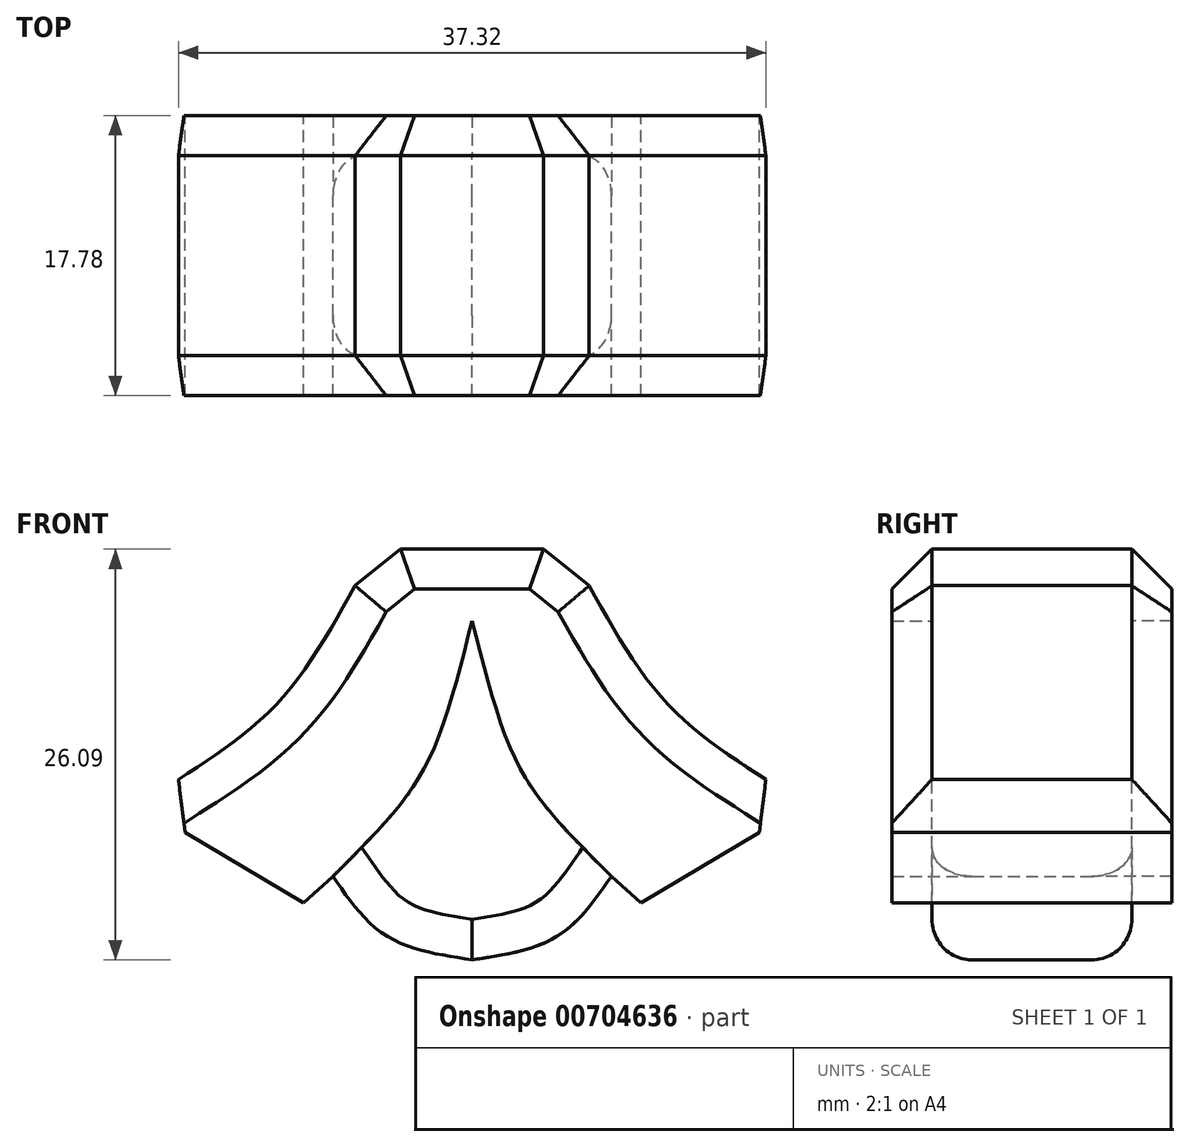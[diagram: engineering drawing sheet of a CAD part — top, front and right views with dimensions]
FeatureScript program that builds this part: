
annotation { "Feature Type Name" : "Feature", "Feature Type Description" : "" }
export const myFeature = defineFeature(function(context is Context, id is Id, definition is map)
    precondition{}
    {
        {
            var Q0;
            Q0=qCreatedBy(makeId("Front.planeOp"),FACE);
            var sketch = newSketch(context, id + "F0", { "sketchPlane" : qUnion([Q0])});
            skFitSpline(sketch, "E0", {"points": [v(-18.66, -145.03) * mm, v(-12.41, -140.25) * mm, v(-7.43, -132.73) * mm], "startDerivative": vector(13.73, 8.78) * mm, "endDerivative": vector(8.77, 15.73) * mm});
            skFitSpline(sketch, "E1", {"points": [v(0, -156.5) * mm, v(-5.42, -154.99) * mm, v(-8.85, -151.2) * mm], "startDerivative": vector(-11.5, 1.7) * mm, "endDerivative": vector(-6.16, 8.95) * mm});
            skFitSpline(sketch, "E2", {"points": [v(-6.32, -27.2) * mm, v(-15.28, -19.21) * mm, v(-26.43, -12.1) * mm, v(-37.33, -8.05) * mm], "startDerivative": vector(-25.96, 24.63) * mm, "endDerivative": vector(-33.62, 10.63) * mm});
            skFitSpline(sketch, "E3", {"points": [v(-37.33, -3.8) * mm, v(-39.84, -2.96) * mm, v(-42.51, -2.04) * mm, v(-42.5, -2) * mm], "startDerivative": vector(-4.66, 1.6) * mm, "endDerivative": vector(0.46, 0.6) * mm});
            skFitSpline(sketch, "E4", {"points": [v(-42.5, -2) * mm, v(-36.56, 4.25) * mm, v(-31.56, 12.84) * mm], "startDerivative": vector(12.98, 12.08) * mm, "endDerivative": vector(8.97, 17.54) * mm});
            skFitSpline(sketch, "E5", {"points": [v(-31.56, 12.84) * mm, v(-28.75, 11.67) * mm, v(-26.43, 10.32) * mm], "startDerivative": vector(5.62, -2.14) * mm, "endDerivative": vector(4.63, -2.93) * mm});
            skFitSpline(sketch, "E6", {"points": [v(-23.95, 12.84) * mm, v(-17.54, 8.59) * mm, v(-10.17, 1.5) * mm], "startDerivative": vector(13.82, -8.22) * mm, "endDerivative": vector(13.74, -14.33) * mm});
            skLineSegment(sketch, "E7", {"start": v(-10.17, 1.5) * mm, "end": v(0, 17.06) * mm});
            skLineSegment(sketch, "E8", {"start": v(0, 17.06) * mm, "end": v(0, 9.54) * mm});
            skLineSegment(sketch, "E9", {"start": v(0, 9.54) * mm, "end": v(0, 17.06) * mm});
            skLineSegment(sketch, "E10", {"start": v(-37.33, -3.8) * mm, "end": v(-37.33, -8.05) * mm});
            skLineSegment(sketch, "E11", {"start": v(-23.95, 12.84) * mm, "end": v(-26.43, 10.32) * mm});
            skLineSegment(sketch, "E12", {"start": v(-6.32, -27.2) * mm, "end": v(0, -29.82) * mm});
            skLineSegment(sketch, "E13", {"start": v(0, -29.82) * mm, "end": v(-6.32, -27.2) * mm});
            skLineSegment(sketch, "E14", {"start": v(-7.43, -132.73) * mm, "end": v(-4.54, -130.41) * mm});
            skLineSegment(sketch, "E15", {"start": v(-4.54, -130.41) * mm, "end": v(0, -130.41) * mm});
            skLineSegment(sketch, "E16", {"start": v(0, -130.41) * mm, "end": v(-4.54, -130.41) * mm});
            skLineSegment(sketch, "E17", {"start": v(-8.85, -151.2) * mm, "end": v(-10.72, -152.9) * mm});
            skLineSegment(sketch, "E18", {"start": v(-10.72, -152.9) * mm, "end": v(-18.24, -148.4) * mm});
            skLineSegment(sketch, "E19", {"start": v(-18.24, -148.4) * mm, "end": v(-18.66, -145.03) * mm});
            skLineSegment(sketch, "E20.MirrorCS", {"start": v(10.17, 1.5) * mm, "end": v(0, 17.06) * mm});
            skFitSpline(sketch, "E21.MirrorCS", {"points": [v(23.95, 12.84) * mm, v(17.54, 8.59) * mm, v(10.17, 1.5) * mm], "startDerivative": vector(-13.82, -8.22) * mm, "endDerivative": vector(-13.74, -14.33) * mm});
            skLineSegment(sketch, "E22.MirrorCS", {"start": v(23.95, 12.84) * mm, "end": v(26.43, 10.32) * mm});
            skFitSpline(sketch, "E23.MirrorCS", {"points": [v(31.56, 12.84) * mm, v(28.75, 11.67) * mm, v(26.43, 10.32) * mm], "startDerivative": vector(-5.62, -2.14) * mm, "endDerivative": vector(-4.63, -2.93) * mm});
            skFitSpline(sketch, "E24.MirrorCS", {"points": [v(42.5, -2) * mm, v(36.56, 4.25) * mm, v(31.56, 12.84) * mm], "startDerivative": vector(-12.98, 12.08) * mm, "endDerivative": vector(-8.97, 17.54) * mm});
            skFitSpline(sketch, "E25.MirrorCS", {"points": [v(37.33, -3.8) * mm, v(39.84, -2.96) * mm, v(42.51, -2.04) * mm, v(42.5, -2) * mm], "startDerivative": vector(4.66, 1.6) * mm, "endDerivative": vector(-0.46, 0.6) * mm});
            skLineSegment(sketch, "E26.MirrorCS", {"start": v(37.33, -3.8) * mm, "end": v(37.33, -8.05) * mm});
            skFitSpline(sketch, "E27.MirrorCS", {"points": [v(6.32, -27.2) * mm, v(15.28, -19.21) * mm, v(26.43, -12.1) * mm, v(37.33, -8.05) * mm], "startDerivative": vector(25.96, 24.63) * mm, "endDerivative": vector(33.62, 10.63) * mm});
            skLineSegment(sketch, "E28.MirrorCS", {"start": v(6.32, -27.2) * mm, "end": v(0, -29.82) * mm});
            skLineSegment(sketch, "E29.MirrorCS", {"start": v(0, -130.41) * mm, "end": v(4.54, -130.41) * mm});
            skLineSegment(sketch, "E30.MirrorCS", {"start": v(7.43, -132.73) * mm, "end": v(4.54, -130.41) * mm});
            skFitSpline(sketch, "E31.MirrorCS", {"points": [v(18.66, -145.03) * mm, v(12.41, -140.25) * mm, v(7.43, -132.73) * mm], "startDerivative": vector(-13.73, 8.78) * mm, "endDerivative": vector(-8.77, 15.73) * mm});
            skLineSegment(sketch, "E32.MirrorCS", {"start": v(18.24, -148.4) * mm, "end": v(18.66, -145.03) * mm});
            skLineSegment(sketch, "E33.MirrorCS", {"start": v(10.72, -152.9) * mm, "end": v(18.24, -148.4) * mm});
            skLineSegment(sketch, "E34.MirrorCS", {"start": v(8.85, -151.2) * mm, "end": v(10.72, -152.9) * mm});
            skFitSpline(sketch, "E35.MirrorCS", {"points": [v(0, -156.5) * mm, v(5.42, -154.99) * mm, v(8.85, -151.2) * mm], "startDerivative": vector(11.5, 1.7) * mm, "endDerivative": vector(6.16, 8.95) * mm});
            skSolve(sketch);
        }
        {
            var Q0;
            Q0=makeQuery(id+"F0.imprint","IMPRINT",FACE,{"disambiguationData":[TD([[makeQuery(id+"F0.imprint","IMPRINT",EDGE,{"derivedFrom":sQuery(id+"F0.wireOp",EDGE,"E2")}),-1.0]])]});
            var Q1;
            Q1=makeQuery(id+"F0.imprint","IMPRINT",FACE,{"disambiguationData":[TD([[makeQuery(id+"F0.imprint","IMPRINT",EDGE,{"derivedFrom":sQuery(id+"F0.wireOp",EDGE,"E0")}),-1.0]])]});
            extrude(context, id + "F1", {"entities" : qUnion([Q0, Q1]), "depth" : 6.35 * mm, "offsetDistance" : 25.4 * mm});
        }
        {
            var Q0;
            Q0=makeQuery(id+"F1.opExtrude","CAP_FACE",FACE,{"disambiguationData":[OSD([sQuery(id+"F0.wireOp",EDGE,"E2"),sQuery(id+"F0.wireOp",EDGE,"E3"),sQuery(id+"F0.wireOp",EDGE,"E4"),sQuery(id+"F0.wireOp",EDGE,"E5"),sQuery(id+"F0.wireOp",EDGE,"E6"),sQuery(id+"F0.wireOp",EDGE,"E7"),sQuery(id+"F0.wireOp",EDGE,"E10"),sQuery(id+"F0.wireOp",EDGE,"E11"),sQuery(id+"F0.wireOp",EDGE,"E13"),sQuery(id+"F0.wireOp",EDGE,"E20.MirrorCS"),sQuery(id+"F0.wireOp",EDGE,"E21.MirrorCS"),sQuery(id+"F0.wireOp",EDGE,"E22.MirrorCS"),sQuery(id+"F0.wireOp",EDGE,"E23.MirrorCS"),sQuery(id+"F0.wireOp",EDGE,"E24.MirrorCS"),sQuery(id+"F0.wireOp",EDGE,"E25.MirrorCS"),sQuery(id+"F0.wireOp",EDGE,"E26.MirrorCS"),sQuery(id+"F0.wireOp",EDGE,"E27.MirrorCS"),sQuery(id+"F0.wireOp",EDGE,"E28.MirrorCS")])],"isStart":true});
            var Q1;
            Q1=makeQuery(id+"F1.opExtrude","CAP_FACE",FACE,{"disambiguationData":[OSD([sQuery(id+"F0.wireOp",EDGE,"E0"),sQuery(id+"F0.wireOp",EDGE,"E1"),sQuery(id+"F0.wireOp",EDGE,"E14"),sQuery(id+"F0.wireOp",EDGE,"E16"),sQuery(id+"F0.wireOp",EDGE,"E17"),sQuery(id+"F0.wireOp",EDGE,"E18"),sQuery(id+"F0.wireOp",EDGE,"E19"),sQuery(id+"F0.wireOp",EDGE,"E29.MirrorCS"),sQuery(id+"F0.wireOp",EDGE,"E30.MirrorCS"),sQuery(id+"F0.wireOp",EDGE,"E31.MirrorCS"),sQuery(id+"F0.wireOp",EDGE,"E32.MirrorCS"),sQuery(id+"F0.wireOp",EDGE,"E33.MirrorCS"),sQuery(id+"F0.wireOp",EDGE,"E34.MirrorCS"),sQuery(id+"F0.wireOp",EDGE,"E35.MirrorCS")])],"isStart":true});
            extrude(context, id + "F2", {"entities" : qUnion([Q0, Q1]), "depth" : 6.35 * mm, "offsetDistance" : 25.4 * mm});
        }
        {
            var Q0;
            Q0=makeQuery(id+"F1.opExtrude","CAP_FACE",FACE,{"disambiguationData":[OSD([sQuery(id+"F0.wireOp",EDGE,"E2"),sQuery(id+"F0.wireOp",EDGE,"E3"),sQuery(id+"F0.wireOp",EDGE,"E4"),sQuery(id+"F0.wireOp",EDGE,"E5"),sQuery(id+"F0.wireOp",EDGE,"E6"),sQuery(id+"F0.wireOp",EDGE,"E7"),sQuery(id+"F0.wireOp",EDGE,"E10"),sQuery(id+"F0.wireOp",EDGE,"E11"),sQuery(id+"F0.wireOp",EDGE,"E13"),sQuery(id+"F0.wireOp",EDGE,"E20.MirrorCS"),sQuery(id+"F0.wireOp",EDGE,"E21.MirrorCS"),sQuery(id+"F0.wireOp",EDGE,"E22.MirrorCS"),sQuery(id+"F0.wireOp",EDGE,"E23.MirrorCS"),sQuery(id+"F0.wireOp",EDGE,"E24.MirrorCS"),sQuery(id+"F0.wireOp",EDGE,"E25.MirrorCS"),sQuery(id+"F0.wireOp",EDGE,"E26.MirrorCS"),sQuery(id+"F0.wireOp",EDGE,"E27.MirrorCS"),sQuery(id+"F0.wireOp",EDGE,"E28.MirrorCS")])],"isStart":false});
            var sketch = newSketch(context, id + "F3", { "sketchPlane" : qUnion([Q0])});
            skFitSpline(sketch, "E36", {"points": [v(-26.43, 10.32) * mm, v(-20.88, 7.37) * mm, v(-15.82, 3.86) * mm, v(-11.19, 0) * mm, v(-9.86, -1.24) * mm], "startDerivative": vector(19.99, -10.01) * mm, "endDerivative": vector(7.2, -6.92) * mm});
            skLineSegment(sketch, "E37", {"start": v(-9.86, -1.24) * mm, "end": v(0, -16.46) * mm});
            skLineSegment(sketch, "E38.MirrorCS", {"start": v(9.86, -1.24) * mm, "end": v(0, -16.46) * mm});
            skFitSpline(sketch, "E39.MirrorCS", {"points": [v(26.43, 10.32) * mm, v(20.88, 7.37) * mm, v(15.82, 3.86) * mm, v(11.19, 0) * mm, v(9.86, -1.24) * mm], "startDerivative": vector(-19.99, -10.01) * mm, "endDerivative": vector(-7.2, -6.92) * mm});
            skLineSegment(sketch, "E40", {"start": v(-10.17, 1.5) * mm, "end": v(-11.19, 0) * mm});
            skLineSegment(sketch, "E41", {"start": v(10.17, 1.5) * mm, "end": v(11.19, 0) * mm});
            skSolve(sketch);
        }
        {
            var Q0;
            {var subQ7=sQuery(id+"F3.wireOp",EDGE,"E37");Q0=makeQuery(id+"F3.imprint","IMPRINT",FACE,{"disambiguationData":[TD([[makeQuery(id+"F3.imprint","IMPRINT",EDGE,{"derivedFrom":subQ7}),-1.0]])]});}
            var Q1;
            {var subQ3=sQuery(id+"F3.wireOp",EDGE,"E37");Q1=makeQuery(id+"F3.imprint","IMPRINT",FACE,{"disambiguationData":[TD([[makeQuery(id+"F3.imprint","IMPRINT",EDGE,{"derivedFrom":subQ3}),1.0]])]});}
            extrude(context, id + "F4", {"entities" : qUnion([Q0, Q1]), "operationType" : NewBodyOperationType.ADD, "depth" : 2.54 * mm, "offsetDistance" : 25.4 * mm});
        }
        {
            var Q0;
            Q0=makeQuery(id+"F4.opExtrude","CAP_FACE",FACE,{"disambiguationData":[OSD([sQuery(id+"F0.wireOp",EDGE,"E2"),sQuery(id+"F0.wireOp",EDGE,"E3"),sQuery(id+"F0.wireOp",EDGE,"E4"),sQuery(id+"F0.wireOp",EDGE,"E5"),sQuery(id+"F0.wireOp",EDGE,"E7"),sQuery(id+"F0.wireOp",EDGE,"E10"),sQuery(id+"F0.wireOp",EDGE,"E13"),sQuery(id+"F0.wireOp",EDGE,"E20.MirrorCS"),sQuery(id+"F0.wireOp",EDGE,"E23.MirrorCS"),sQuery(id+"F0.wireOp",EDGE,"E24.MirrorCS"),sQuery(id+"F0.wireOp",EDGE,"E25.MirrorCS"),sQuery(id+"F0.wireOp",EDGE,"E26.MirrorCS"),sQuery(id+"F0.wireOp",EDGE,"E27.MirrorCS"),sQuery(id+"F0.wireOp",EDGE,"E28.MirrorCS"),sQuery(id+"F3.wireOp",EDGE,"E36"),sQuery(id+"F3.wireOp",EDGE,"E39.MirrorCS"),sQuery(id+"F3.wireOp",EDGE,"E40"),sQuery(id+"F3.wireOp",EDGE,"E41")])],"isStart":false});
            extrude(context, id + "F5", {"entities" : qUnion([Q0]), "oppositeDirection" : true, "depth" : 17.78 * mm, "offsetDistance" : 25.4 * mm});
        }
        {
            var Q0;
            Q0=makeQuery(id+"F5.opExtrude","CAP_FACE",FACE,{"disambiguationData":[OSD([sQuery(id+"F0.wireOp",EDGE,"E2"),sQuery(id+"F0.wireOp",EDGE,"E3"),sQuery(id+"F0.wireOp",EDGE,"E4"),sQuery(id+"F0.wireOp",EDGE,"E5"),sQuery(id+"F0.wireOp",EDGE,"E7"),sQuery(id+"F0.wireOp",EDGE,"E10"),sQuery(id+"F0.wireOp",EDGE,"E13"),sQuery(id+"F0.wireOp",EDGE,"E20.MirrorCS"),sQuery(id+"F0.wireOp",EDGE,"E23.MirrorCS"),sQuery(id+"F0.wireOp",EDGE,"E24.MirrorCS"),sQuery(id+"F0.wireOp",EDGE,"E25.MirrorCS"),sQuery(id+"F0.wireOp",EDGE,"E26.MirrorCS"),sQuery(id+"F0.wireOp",EDGE,"E27.MirrorCS"),sQuery(id+"F0.wireOp",EDGE,"E28.MirrorCS"),sQuery(id+"F3.wireOp",EDGE,"E36"),sQuery(id+"F3.wireOp",EDGE,"E39.MirrorCS"),sQuery(id+"F3.wireOp",EDGE,"E40"),sQuery(id+"F3.wireOp",EDGE,"E41")])],"isStart":true});
            var sketch = newSketch(context, id + "F6", { "sketchPlane" : qUnion([Q0])});
            skLineSegment(sketch, "E42", {"start": v(-11.19, 0) * mm, "end": v(0, -16.42) * mm});
            skLineSegment(sketch, "E43", {"start": v(0, -16.42) * mm, "end": v(11.19, 0) * mm});
            skSolve(sketch);
        }
        {
            var Q0;
            Q0=makeQuery(id+"F6.imprint","IMPRINT",FACE,{"disambiguationData":[TD([[makeQuery(id+"F6.imprint","IMPRINT",EDGE,{"derivedFrom":sQuery(id+"F6.wireOp",EDGE,"E42")}),-1.0]])]});
            var sketch = newSketch(context, id + "F7", { "sketchPlane" : qUnion([Q0])});
            skLineSegment(sketch, "E44", {"start": v(0, -16.57) * mm, "end": v(-11.35, 0) * mm});
            skLineSegment(sketch, "E45", {"start": v(-11.35, 0) * mm, "end": v(0, -16.57) * mm});
            skLineSegment(sketch, "E46.MirrorCS", {"start": v(11.35, 0) * mm, "end": v(0, -16.57) * mm});
            skSolve(sketch);
        }
        {
            var Q0;
            Q0=makeQuery(id+"F7.imprint","IMPRINT",FACE,{"disambiguationData":[TD([[makeQuery(id+"F7.imprint","IMPRINT",EDGE,{"derivedFrom":makeQuery(id+"F6.imprint","IMPRINT",EDGE,{"derivedFrom":sQuery(id+"F6.wireOp",EDGE,"E42")})}),-1.0]])]});
            var Q1;
            Q1=makeQuery(id+"F6.imprint","IMPRINT",FACE,{"disambiguationData":[TD([[makeQuery(id+"F6.imprint","IMPRINT",EDGE,{"derivedFrom":sQuery(id+"F6.wireOp",EDGE,"E42")}),1.0]])]});
            var Q2;
            {var subQ0=sQuery(id+"F0.wireOp",EDGE,"E23.MirrorCS");var subQ1=sQuery(id+"F0.wireOp",EDGE,"E22.MirrorCS");var subQ2=sQuery(id+"F0.wireOp",EDGE,"E21.MirrorCS");var subQ3=sQuery(id+"F0.wireOp",EDGE,"E20.MirrorCS");Q2=makeQuery(id+"F4.boolean.opBoolean","SPLIT",FACE,{"disambiguationData":[TD([makeQuery(id+"F1.opExtrude","SWEPT_FACE",FACE,{"disambiguationData":[OSD([subQ3])]})])],"derivedFrom":makeQuery(id+"F1.opExtrude","CAP_FACE",FACE,{"disambiguationData":[OSD([sQuery(id+"F0.wireOp",EDGE,"E2"),sQuery(id+"F0.wireOp",EDGE,"E3"),sQuery(id+"F0.wireOp",EDGE,"E4"),sQuery(id+"F0.wireOp",EDGE,"E5"),sQuery(id+"F0.wireOp",EDGE,"E6"),sQuery(id+"F0.wireOp",EDGE,"E7"),sQuery(id+"F0.wireOp",EDGE,"E10"),sQuery(id+"F0.wireOp",EDGE,"E11"),sQuery(id+"F0.wireOp",EDGE,"E13"),subQ3,subQ2,subQ1,subQ0,sQuery(id+"F0.wireOp",EDGE,"E24.MirrorCS"),sQuery(id+"F0.wireOp",EDGE,"E25.MirrorCS"),sQuery(id+"F0.wireOp",EDGE,"E26.MirrorCS"),sQuery(id+"F0.wireOp",EDGE,"E27.MirrorCS"),sQuery(id+"F0.wireOp",EDGE,"E28.MirrorCS")])],"isStart":false})});}
            var Q3;
            {var subQ0=sQuery(id+"F0.wireOp",EDGE,"E11");var subQ1=sQuery(id+"F0.wireOp",EDGE,"E7");var subQ2=sQuery(id+"F0.wireOp",EDGE,"E6");var subQ3=sQuery(id+"F0.wireOp",EDGE,"E5");Q3=makeQuery(id+"F4.boolean.opBoolean","SPLIT",FACE,{"disambiguationData":[TD([makeQuery(id+"F1.opExtrude","SWEPT_FACE",FACE,{"disambiguationData":[OSD([subQ3])]})])],"derivedFrom":makeQuery(id+"F1.opExtrude","CAP_FACE",FACE,{"disambiguationData":[OSD([sQuery(id+"F0.wireOp",EDGE,"E2"),sQuery(id+"F0.wireOp",EDGE,"E3"),sQuery(id+"F0.wireOp",EDGE,"E4"),subQ3,subQ2,subQ1,sQuery(id+"F0.wireOp",EDGE,"E10"),subQ0,sQuery(id+"F0.wireOp",EDGE,"E13"),sQuery(id+"F0.wireOp",EDGE,"E20.MirrorCS"),sQuery(id+"F0.wireOp",EDGE,"E21.MirrorCS"),sQuery(id+"F0.wireOp",EDGE,"E22.MirrorCS"),sQuery(id+"F0.wireOp",EDGE,"E23.MirrorCS"),sQuery(id+"F0.wireOp",EDGE,"E24.MirrorCS"),sQuery(id+"F0.wireOp",EDGE,"E25.MirrorCS"),sQuery(id+"F0.wireOp",EDGE,"E26.MirrorCS"),sQuery(id+"F0.wireOp",EDGE,"E27.MirrorCS"),sQuery(id+"F0.wireOp",EDGE,"E28.MirrorCS")])],"isStart":false})});}
            extrude(context, id + "F8", {"entities" : qUnion([Q0, Q1, Q2, Q3]), "operationType" : NewBodyOperationType.REMOVE, "oppositeDirection" : true, "depth" : 25.4 * mm, "offsetDistance" : 25.4 * mm});
        }
        {
            var Q0;
            Q0=makeQuery(id+"F1.opExtrude","CAP_FACE",FACE,{"disambiguationData":[OSD([sQuery(id+"F0.wireOp",EDGE,"E0"),sQuery(id+"F0.wireOp",EDGE,"E1"),sQuery(id+"F0.wireOp",EDGE,"E14"),sQuery(id+"F0.wireOp",EDGE,"E16"),sQuery(id+"F0.wireOp",EDGE,"E17"),sQuery(id+"F0.wireOp",EDGE,"E18"),sQuery(id+"F0.wireOp",EDGE,"E19"),sQuery(id+"F0.wireOp",EDGE,"E29.MirrorCS"),sQuery(id+"F0.wireOp",EDGE,"E30.MirrorCS"),sQuery(id+"F0.wireOp",EDGE,"E31.MirrorCS"),sQuery(id+"F0.wireOp",EDGE,"E32.MirrorCS"),sQuery(id+"F0.wireOp",EDGE,"E33.MirrorCS"),sQuery(id+"F0.wireOp",EDGE,"E34.MirrorCS"),sQuery(id+"F0.wireOp",EDGE,"E35.MirrorCS")])],"isStart":false});
            var sketch = newSketch(context, id + "F9", { "sketchPlane" : qUnion([Q0])});
            skFitSpline(sketch, "E47", {"points": [v(-8.85, -151.2) * mm, v(-4.84, -146.96) * mm, v(-2.35, -142.88) * mm, v(0, -134.96) * mm], "startDerivative": vector(13.35, 13.26) * mm, "endDerivative": vector(5.68, 22.53) * mm});
            skFitSpline(sketch, "E48.MirrorCS", {"points": [v(8.85, -151.2) * mm, v(4.84, -146.96) * mm, v(2.35, -142.88) * mm, v(0, -134.96) * mm], "startDerivative": vector(-13.35, 13.26) * mm, "endDerivative": vector(-5.68, 22.53) * mm});
            skSolve(sketch);
        }
        {
            var Q0;
            Q0=makeQuery(id+"F9.imprint","IMPRINT",FACE,{"disambiguationData":[TD([[makeQuery(id+"F9.imprint","IMPRINT",EDGE,{"derivedFrom":sQuery(id+"F9.wireOp",EDGE,"E47")}),1.0]])]});
            extrude(context, id + "F10", {"entities" : qUnion([Q0]), "operationType" : NewBodyOperationType.ADD, "depth" : 2.54 * mm, "offsetDistance" : 25.4 * mm});
        }
        {
            var Q0;
            Q0=makeQuery(id+"F10.opExtrude","CAP_FACE",FACE,{"disambiguationData":[OSD([sQuery(id+"F0.wireOp",EDGE,"E0"),sQuery(id+"F0.wireOp",EDGE,"E14"),sQuery(id+"F0.wireOp",EDGE,"E16"),sQuery(id+"F0.wireOp",EDGE,"E17"),sQuery(id+"F0.wireOp",EDGE,"E18"),sQuery(id+"F0.wireOp",EDGE,"E19"),sQuery(id+"F0.wireOp",EDGE,"E29.MirrorCS"),sQuery(id+"F0.wireOp",EDGE,"E30.MirrorCS"),sQuery(id+"F0.wireOp",EDGE,"E31.MirrorCS"),sQuery(id+"F0.wireOp",EDGE,"E32.MirrorCS"),sQuery(id+"F0.wireOp",EDGE,"E33.MirrorCS"),sQuery(id+"F0.wireOp",EDGE,"E34.MirrorCS"),sQuery(id+"F9.wireOp",EDGE,"E47"),sQuery(id+"F9.wireOp",EDGE,"E48.MirrorCS")])],"isStart":false});
            extrude(context, id + "F11", {"entities" : qUnion([Q0]), "operationType" : NewBodyOperationType.ADD, "oppositeDirection" : true, "depth" : 17.78 * mm, "offsetDistance" : 25.4 * mm});
        }
        {
            var Q0;
            Q0=makeQuery(id+"F10.opExtrude","CAP_EDGE",EDGE,{"disambiguationData":[OSD([sQuery(id+"F0.wireOp",EDGE,"E0")])],"isStart":false});
            var Q1;
            Q1=makeQuery(id+"F10.opExtrude","CAP_EDGE",EDGE,{"disambiguationData":[OSD([sQuery(id+"F0.wireOp",EDGE,"E14")])],"isStart":false});
            var Q2;
            Q2=makeQuery(id+"F10.opExtrude","CAP_EDGE",EDGE,{"disambiguationData":[OSD([sQuery(id+"F0.wireOp",EDGE,"E16"),sQuery(id+"F0.wireOp",EDGE,"E29.MirrorCS")])],"isStart":false});
            var Q3;
            Q3=makeQuery(id+"F10.opExtrude","CAP_EDGE",EDGE,{"disambiguationData":[OSD([sQuery(id+"F0.wireOp",EDGE,"E30.MirrorCS")])],"isStart":false});
            var Q4;
            Q4=makeQuery(id+"F10.opExtrude","CAP_EDGE",EDGE,{"disambiguationData":[OSD([sQuery(id+"F0.wireOp",EDGE,"E31.MirrorCS")])],"isStart":false});
            var Q5;
            Q5=makeQuery(id+"F11.opExtrude","CAP_EDGE",EDGE,{"disambiguationData":[OSD([sQuery(id+"F0.wireOp",EDGE,"E31.MirrorCS")])],"isStart":false});
            var Q6;
            Q6=makeQuery(id+"F11.opExtrude","CAP_EDGE",EDGE,{"disambiguationData":[OSD([sQuery(id+"F0.wireOp",EDGE,"E30.MirrorCS")])],"isStart":false});
            var Q7;
            Q7=makeQuery(id+"F11.opExtrude","CAP_EDGE",EDGE,{"disambiguationData":[OSD([sQuery(id+"F0.wireOp",EDGE,"E16"),sQuery(id+"F0.wireOp",EDGE,"E29.MirrorCS")])],"isStart":false});
            var Q8;
            Q8=makeQuery(id+"F11.opExtrude","CAP_EDGE",EDGE,{"disambiguationData":[OSD([sQuery(id+"F0.wireOp",EDGE,"E14")])],"isStart":false});
            var Q9;
            Q9=makeQuery(id+"F11.opExtrude","CAP_EDGE",EDGE,{"disambiguationData":[OSD([sQuery(id+"F0.wireOp",EDGE,"E0")])],"isStart":false});
            chamfer(context, id + "F12", {"entities" : qUnion([Q0, Q1, Q2, Q3, Q4, Q5, Q6, Q7, Q8, Q9]), "width" : 2.54 * mm, "tangentPropagation" : true});
        }
        {
            var Q0;
            Q0=makeQuery(id+"F1.opExtrude","CAP_EDGE",EDGE,{"disambiguationData":[OSD([sQuery(id+"F0.wireOp",EDGE,"E1")])],"isStart":false});
            var Q1;
            Q1=makeQuery(id+"F1.opExtrude","CAP_EDGE",EDGE,{"disambiguationData":[OSD([sQuery(id+"F0.wireOp",EDGE,"E35.MirrorCS")])],"isStart":false});
            var Q2;
            Q2=makeQuery(id+"F2.opExtrude","CAP_EDGE",EDGE,{"disambiguationData":[OSD([sQuery(id+"F0.wireOp",EDGE,"E1")])],"isStart":false});
            var Q3;
            Q3=makeQuery(id+"F2.opExtrude","CAP_EDGE",EDGE,{"disambiguationData":[OSD([sQuery(id+"F0.wireOp",EDGE,"E35.MirrorCS")])],"isStart":false});
            fillet(context, id + "F13", {"entities" : qUnion([Q0, Q1, Q2, Q3]), "radius" : 2.54 * mm, "tangentPropagation" : true, "allowEdgeOverflow" : false});
        }
    });
